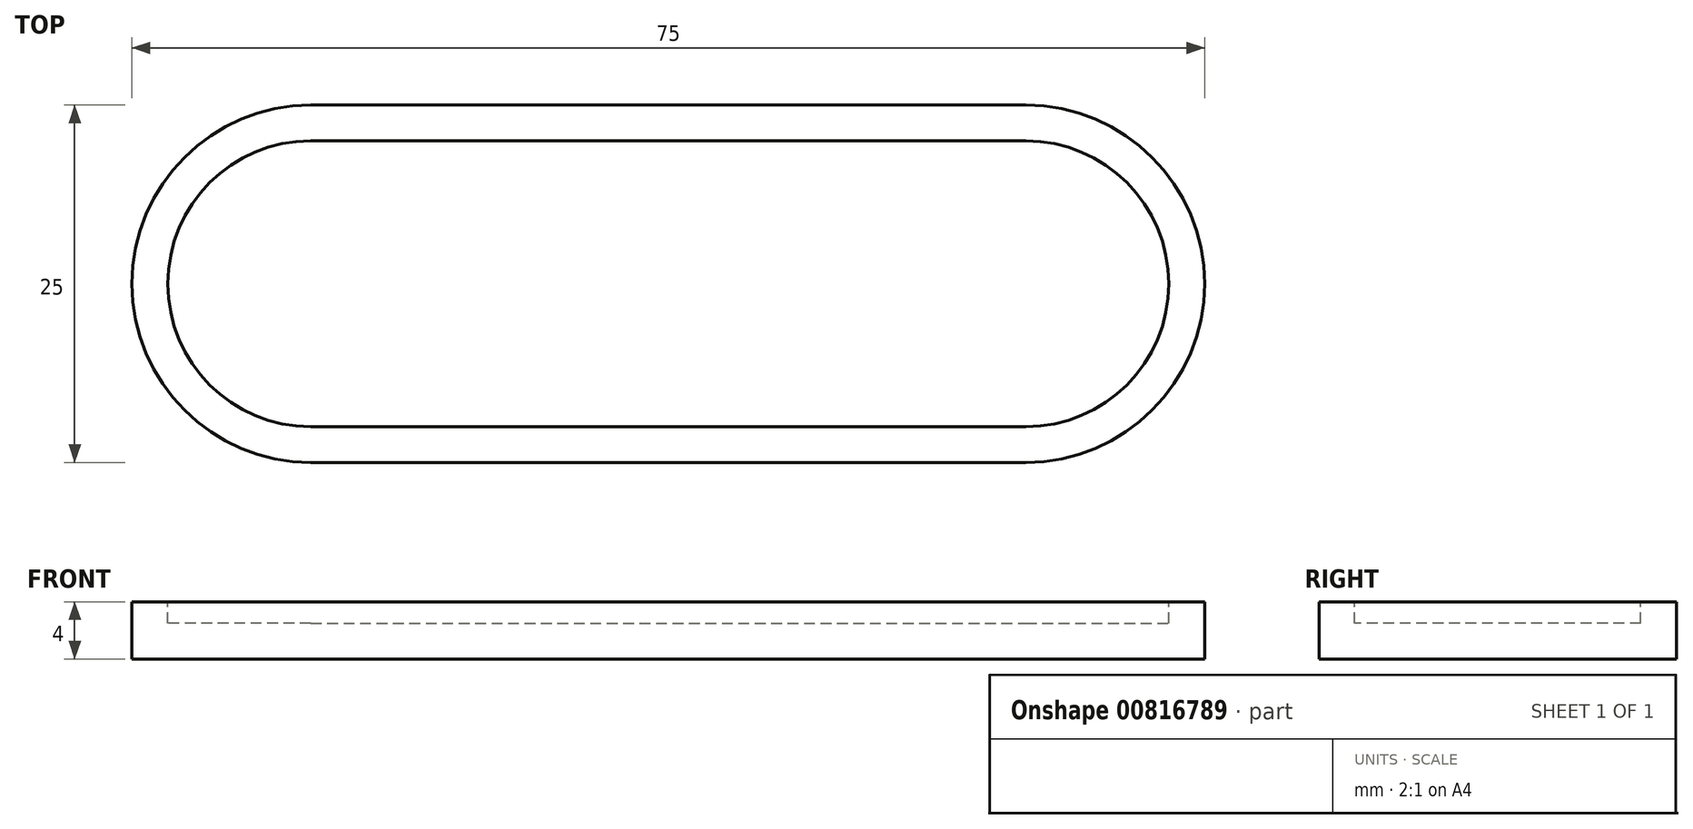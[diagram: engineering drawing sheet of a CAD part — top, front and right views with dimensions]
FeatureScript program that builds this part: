
annotation { "Feature Type Name" : "Feature", "Feature Type Description" : "" }
export const myFeature = defineFeature(function(context is Context, id is Id, definition is map)
    precondition{}
    {
        {
            var Q0;
            Q0=qCreatedBy(makeId("Top.planeOp"),FACE);
            var sketch = newSketch(context, id + "F0", { "sketchPlane" : qUnion([Q0])});
            skLineSegment(sketch, "E0.bottom", {"start": v(12.5, 0) * mm, "end": v(62.5, 0) * mm});
            skLineSegment(sketch, "E0.top", {"start": v(12.5, 25) * mm, "end": v(62.5, 25) * mm});
            skArc(sketch, "E1", {"start": v(12.5, 25) * mm, "mid": v(0, 12.5) * mm, "end": v(12.5, 0) * mm});
            skPoint(sketch, "E1.centerSnap0", {"position": v(0, 12.5) * mm});
            skArc(sketch, "E2", {"start": v(62.5, 0) * mm, "mid": v(75, 12.5) * mm, "end": v(62.5, 25) * mm});
            skPoint(sketch, "E2.centerSnap0", {"position": v(75, 12.5) * mm});
            skPoint(sketch, "E3.orphan", {"position": v(0, 25) * mm});
            skPoint(sketch, "E4.orphan", {"position": v(0, 0) * mm});
            skPoint(sketch, "E5.orphan", {"position": v(75, 25) * mm});
            skPoint(sketch, "E6.orphan", {"position": v(75, 0) * mm});
            skSolve(sketch);
        }
        {
            var Q0;
            Q0=makeQuery(id+"F0.imprint","IMPRINT",FACE,{"disambiguationData":[TD([[makeQuery(id+"F0.imprint","IMPRINT",EDGE,{"derivedFrom":sQuery(id+"F0.wireOp",EDGE,"E0.bottom")}),1.0]])]});
            extrude(context, id + "F1", {"entities" : qUnion([Q0]), "depth" : 4 * mm, "offsetDistance" : 25 * mm});
        }
        {
            var Q0;
            Q0=makeQuery(id+"F1.opExtrude","CAP_FACE",FACE,{"disambiguationData":[OSD([sQuery(id+"F0.wireOp",EDGE,"E0.bottom"),sQuery(id+"F0.wireOp",EDGE,"E0.top"),sQuery(id+"F0.wireOp",EDGE,"E1"),sQuery(id+"F0.wireOp",EDGE,"E2")])],"isStart":false});
            var sketch = newSketch(context, id + "F2", { "sketchPlane" : qUnion([Q0])});
            skArc(sketch, "E7", {"start": v(12.5, 22.5) * mm, "mid": v(2.5, 12.5) * mm, "end": v(12.5, 2.5) * mm});
            skArc(sketch, "E8", {"start": v(62.5, 2.5) * mm, "mid": v(72.5, 12.5) * mm, "end": v(62.5, 22.5) * mm});
            skLineSegment(sketch, "E9", {"start": v(12.5, 22.5) * mm, "end": v(62.5, 22.5) * mm});
            skLineSegment(sketch, "E10", {"start": v(12.5, 2.5) * mm, "end": v(62.5, 2.5) * mm});
            skSolve(sketch);
        }
        {
            var Q0;
            Q0=makeQuery(id+"F2.imprint","IMPRINT",FACE,{"disambiguationData":[TD([[makeQuery(id+"F2.imprint","IMPRINT",EDGE,{"derivedFrom":sQuery(id+"F2.wireOp",EDGE,"E7")}),1.0]])]});
            extrude(context, id + "F3", {"entities" : qUnion([Q0]), "operationType" : NewBodyOperationType.REMOVE, "oppositeDirection" : true, "depth" : 1.5 * mm, "offsetDistance" : 25 * mm});
        }
    });
